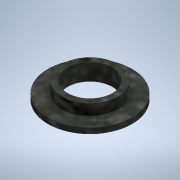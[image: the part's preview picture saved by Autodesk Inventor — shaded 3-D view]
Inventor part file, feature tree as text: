
AUTODESK INVENTOR PART (.ipt)
format: ipt  version: 2020.2 (Build 242310000, 310)  size: 116,224 bytes
history: native  units: mm
features: extrude x2, other x1, sketch x1
ambient origin geometry x8: Origin, YZ Plane, XZ Plane, XY Plane, X Axis, Y Axis, Z Axis, Center Point
bodies: Body1 (feature_tree)
feature tree (4):
  other  "ソリッド1"
  sketch  "スケッチ1"
  extrude  "押し出し1"  Depth=8.0mm
  extrude  "押し出し2"  Depth=10.0mm
